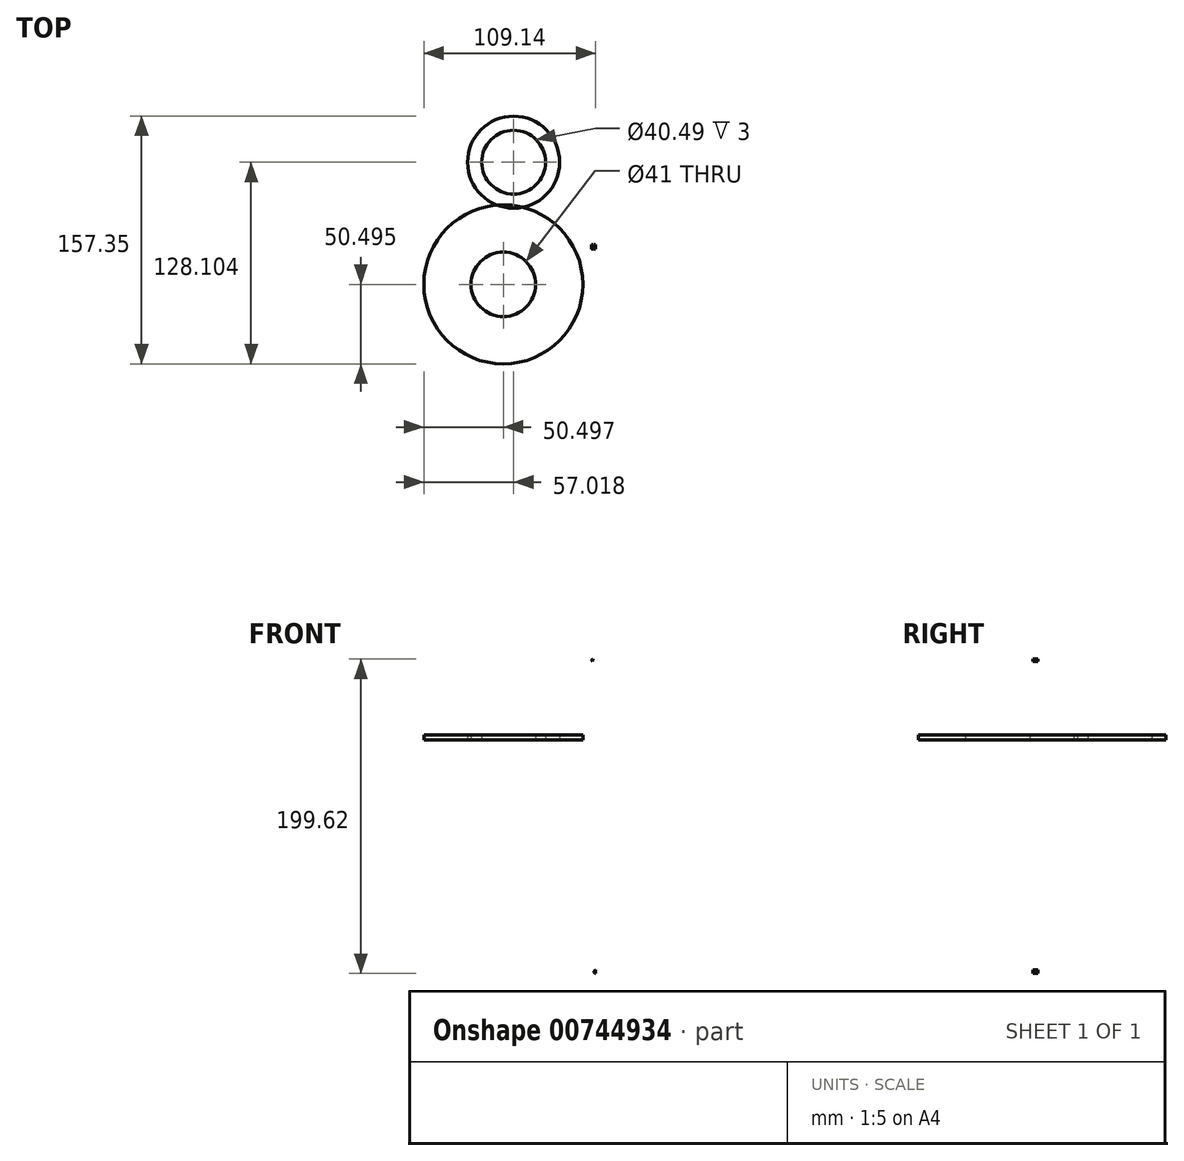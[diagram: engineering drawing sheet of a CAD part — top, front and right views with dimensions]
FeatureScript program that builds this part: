
annotation { "Feature Type Name" : "Feature", "Feature Type Description" : "" }
export const myFeature = defineFeature(function(context is Context, id is Id, definition is map)
    precondition{}
    {
        {
            var Q0;
            Q0=qCreatedBy(makeId("Front.planeOp"),FACE);
            var sketch = newSketch(context, id + "F0", { "sketchPlane" : qUnion([Q0])});
            skFitSpline(sketch, "E0", {"points": [v(18.94, 55.8) * mm, v(19.4, 42.74) * mm, v(74.56, -23) * mm, v(58.26, -54.69) * mm, v(18.93, -151.45) * mm], "startDerivative": vector(-29.4, -78.93) * mm, "endDerivative": vector(0, -157.02) * mm});
            skFitSpline(sketch, "E1.0", {"points": [v(9.57, 59.29) * mm, v(9.44, 58.92) * mm, v(9.1, 58.03) * mm, v(8.45, 56.18) * mm, v(7.84, 53.83) * mm, v(7.44, 51.02) * mm, v(7.45, 47.87) * mm, v(7.89, 45.1) * mm, v(8.5, 42.89) * mm, v(9.08, 41.22) * mm, v(9.67, 39.84) * mm, v(10.2, 38.74) * mm, v(10.64, 37.9) * mm, v(11.1, 37.1) * mm, v(11.72, 36.02) * mm, v(12.56, 34.7) * mm, v(13.65, 33.11) * mm, v(15.19, 31) * mm, v(17.29, 28.36) * mm, v(20.06, 25.1) * mm, v(23.05, 21.77) * mm, v(27.29, 17.22) * mm, v(32.95, 11.36) * mm, v(39.98, 4.2) * mm, v(46.9, -2.94) * mm, v(53.3, -9.85) * mm, v(57.89, -15.23) * mm, v(60.89, -19.14) * mm, v(62.74, -21.82) * mm, v(63.91, -23.77) * mm, v(64.6, -25.1) * mm, v(64.93, -25.82) * mm, v(65.13, -26.31) * mm, v(65.28, -26.74) * mm, v(65.42, -27.2) * mm, v(65.51, -27.62) * mm, v(65.56, -28.04) * mm, v(65.56, -28.36) * mm, v(65.5, -28.75) * mm, v(65.26, -29.42) * mm, v(64.73, -30.46) * mm, v(63.8, -31.88) * mm, v(62.48, -33.62) * mm, v(60.8, -35.67) * mm, v(58.8, -38.02) * mm, v(56.54, -40.67) * mm, v(54.08, -43.65) * mm, v(51.92, -46.42) * mm, v(50.14, -48.83) * mm, v(48.36, -51.35) * mm, v(46.15, -54.66) * mm, v(43.52, -58.88) * mm, v(40.9, -63.31) * mm, v(37.47, -69.48) * mm, v(33.27, -77.6) * mm, v(28.46, -87.76) * mm, v(23.96, -98.1) * mm, v(19.86, -108.39) * mm, v(16.26, -118.37) * mm, v(13.25, -127.84) * mm, v(11.3, -135.12) * mm, v(10.14, -140.51) * mm, v(9.48, -144.34) * mm, v(9.04, -147.97) * mm, v(8.93, -150.3) * mm, v(8.93, -151.45) * mm]});
            skLineSegment(sketch, "E2", {"start": v(18.94, 55.8) * mm, "end": v(8.37, 55.8) * mm});
            skLineSegment(sketch, "E3", {"start": v(18.93, -151.45) * mm, "end": v(8.93, -151.45) * mm});
            skLineSegment(sketch, "E4", {"start": v(14.05, 32.57) * mm, "end": v(16.18, 32.57) * mm});
            skFitSpline(sketch, "E5.trimOffspring", {"points": [v(9.57, 59.29) * mm, v(9.44, 58.92) * mm, v(9.1, 58.03) * mm, v(8.45, 56.18) * mm, v(7.84, 53.83) * mm, v(7.44, 51.02) * mm, v(7.45, 47.87) * mm, v(7.89, 45.1) * mm, v(8.5, 42.89) * mm, v(9.08, 41.22) * mm, v(9.67, 39.84) * mm, v(10.2, 38.74) * mm, v(10.64, 37.9) * mm, v(11.1, 37.1) * mm, v(11.72, 36.02) * mm, v(12.56, 34.7) * mm, v(13.65, 33.11) * mm, v(15.19, 31) * mm, v(17.29, 28.36) * mm, v(20.06, 25.1) * mm, v(23.05, 21.77) * mm, v(27.29, 17.22) * mm, v(32.95, 11.36) * mm, v(39.98, 4.2) * mm, v(46.9, -2.94) * mm, v(53.3, -9.85) * mm, v(57.89, -15.23) * mm, v(60.89, -19.14) * mm, v(62.74, -21.82) * mm, v(63.91, -23.77) * mm, v(64.6, -25.1) * mm, v(64.93, -25.82) * mm, v(65.13, -26.31) * mm, v(65.28, -26.74) * mm, v(65.42, -27.2) * mm, v(65.51, -27.62) * mm, v(65.56, -28.04) * mm, v(65.56, -28.36) * mm, v(65.5, -28.75) * mm, v(65.26, -29.42) * mm, v(64.73, -30.46) * mm, v(63.8, -31.88) * mm, v(62.48, -33.62) * mm, v(60.8, -35.67) * mm, v(58.8, -38.02) * mm, v(56.54, -40.67) * mm, v(54.08, -43.65) * mm, v(51.92, -46.42) * mm, v(50.14, -48.83) * mm, v(48.36, -51.35) * mm, v(46.15, -54.66) * mm, v(43.52, -58.88) * mm, v(40.9, -63.31) * mm, v(37.47, -69.48) * mm, v(33.27, -77.6) * mm, v(28.46, -87.76) * mm, v(23.96, -98.1) * mm, v(19.86, -108.39) * mm, v(16.26, -118.37) * mm, v(13.25, -127.84) * mm, v(11.3, -135.12) * mm, v(10.14, -140.51) * mm, v(9.48, -144.34) * mm, v(9.04, -147.97) * mm, v(8.93, -150.3) * mm, v(8.93, -151.45) * mm]});
            skFitSpline(sketch, "E6.trimOffspring", {"points": [v(9.57, 59.29) * mm, v(9.44, 58.92) * mm, v(9.1, 58.03) * mm, v(8.45, 56.18) * mm, v(7.84, 53.83) * mm, v(7.44, 51.02) * mm, v(7.45, 47.87) * mm, v(7.89, 45.1) * mm, v(8.5, 42.89) * mm, v(9.08, 41.22) * mm, v(9.67, 39.84) * mm, v(10.2, 38.74) * mm, v(10.64, 37.9) * mm, v(11.1, 37.1) * mm, v(11.72, 36.02) * mm, v(12.56, 34.7) * mm, v(13.65, 33.11) * mm, v(15.19, 31) * mm, v(17.29, 28.36) * mm, v(20.06, 25.1) * mm, v(23.05, 21.77) * mm, v(27.29, 17.22) * mm, v(32.95, 11.36) * mm, v(39.98, 4.2) * mm, v(46.9, -2.94) * mm, v(53.3, -9.85) * mm, v(57.89, -15.23) * mm, v(60.89, -19.14) * mm, v(62.74, -21.82) * mm, v(63.91, -23.77) * mm, v(64.6, -25.1) * mm, v(64.93, -25.82) * mm, v(65.13, -26.31) * mm, v(65.28, -26.74) * mm, v(65.42, -27.2) * mm, v(65.51, -27.62) * mm, v(65.56, -28.04) * mm, v(65.56, -28.36) * mm, v(65.5, -28.75) * mm, v(65.26, -29.42) * mm, v(64.73, -30.46) * mm, v(63.8, -31.88) * mm, v(62.48, -33.62) * mm, v(60.8, -35.67) * mm, v(58.8, -38.02) * mm, v(56.54, -40.67) * mm, v(54.08, -43.65) * mm, v(51.92, -46.42) * mm, v(50.14, -48.83) * mm, v(48.36, -51.35) * mm, v(46.15, -54.66) * mm, v(43.52, -58.88) * mm, v(40.9, -63.31) * mm, v(37.47, -69.48) * mm, v(33.27, -77.6) * mm, v(28.46, -87.76) * mm, v(23.96, -98.1) * mm, v(19.86, -108.39) * mm, v(16.26, -118.37) * mm, v(13.25, -127.84) * mm, v(11.3, -135.12) * mm, v(10.14, -140.51) * mm, v(9.48, -144.34) * mm, v(9.04, -147.97) * mm, v(8.93, -150.3) * mm, v(8.93, -151.45) * mm]});
            skLineSegment(sketch, "E7", {"start": v(42.73, 1.36) * mm, "end": v(42.73, 1.36) * mm});
            skPoint(sketch, "E8.orphan", {"position": v(0, -86.14) * mm});
            skPoint(sketch, "E9.end.orphan", {"position": v(15.52, -133.04) * mm});
            skFitSpline(sketch, "E10.trimOffspring", {"points": [v(9.57, 59.29) * mm, v(9.44, 58.92) * mm, v(9.1, 58.03) * mm, v(8.45, 56.18) * mm, v(7.84, 53.83) * mm, v(7.44, 51.02) * mm, v(7.45, 47.87) * mm, v(7.89, 45.1) * mm, v(8.5, 42.89) * mm, v(9.08, 41.22) * mm, v(9.67, 39.84) * mm, v(10.2, 38.74) * mm, v(10.64, 37.9) * mm, v(11.1, 37.1) * mm, v(11.72, 36.02) * mm, v(12.56, 34.7) * mm, v(13.65, 33.11) * mm, v(15.19, 31) * mm, v(17.29, 28.36) * mm, v(20.06, 25.1) * mm, v(23.05, 21.77) * mm, v(27.29, 17.22) * mm, v(32.95, 11.36) * mm, v(39.98, 4.2) * mm, v(46.9, -2.94) * mm, v(53.3, -9.85) * mm, v(57.89, -15.23) * mm, v(60.89, -19.14) * mm, v(62.74, -21.82) * mm, v(63.91, -23.77) * mm, v(64.6, -25.1) * mm, v(64.93, -25.82) * mm, v(65.13, -26.31) * mm, v(65.28, -26.74) * mm, v(65.42, -27.2) * mm, v(65.51, -27.62) * mm, v(65.56, -28.04) * mm, v(65.56, -28.36) * mm, v(65.5, -28.75) * mm, v(65.26, -29.42) * mm, v(64.73, -30.46) * mm, v(63.8, -31.88) * mm, v(62.48, -33.62) * mm, v(60.8, -35.67) * mm, v(58.8, -38.02) * mm, v(56.54, -40.67) * mm, v(54.08, -43.65) * mm, v(51.92, -46.42) * mm, v(50.14, -48.83) * mm, v(48.36, -51.35) * mm, v(46.15, -54.66) * mm, v(43.52, -58.88) * mm, v(40.9, -63.31) * mm, v(37.47, -69.48) * mm, v(33.27, -77.6) * mm, v(28.46, -87.76) * mm, v(23.96, -98.1) * mm, v(19.86, -108.39) * mm, v(16.26, -118.37) * mm, v(13.25, -127.84) * mm, v(11.3, -135.12) * mm, v(10.14, -140.51) * mm, v(9.48, -144.34) * mm, v(9.04, -147.97) * mm, v(8.93, -150.3) * mm, v(8.93, -151.45) * mm]});
            skLineSegment(sketch, "E11", {"start": v(14.05, 32.57) * mm, "end": v(21.01, 32.57) * mm});
            skLineSegment(sketch, "E12", {"start": v(21.01, 32.57) * mm, "end": v(21.01, 29.66) * mm});
            skLineSegment(sketch, "E13", {"start": v(21.01, 29.66) * mm, "end": v(16.36, 29.66) * mm});
            skLineSegment(sketch, "E14", {"start": v(59.17, -16.92) * mm, "end": v(59.17, -16.92) * mm});
            skFitSpline(sketch, "E15.trimOffspring", {"points": [v(9.57, 59.29) * mm, v(9.44, 58.92) * mm, v(9.1, 58.03) * mm, v(8.45, 56.18) * mm, v(7.84, 53.83) * mm, v(7.44, 51.02) * mm, v(7.45, 47.87) * mm, v(7.89, 45.1) * mm, v(8.5, 42.89) * mm, v(9.08, 41.22) * mm, v(9.67, 39.84) * mm, v(10.2, 38.74) * mm, v(10.64, 37.9) * mm, v(11.1, 37.1) * mm, v(11.72, 36.02) * mm, v(12.56, 34.7) * mm, v(13.65, 33.11) * mm, v(15.19, 31) * mm, v(17.29, 28.36) * mm, v(20.06, 25.1) * mm, v(23.05, 21.77) * mm, v(27.29, 17.22) * mm, v(32.95, 11.36) * mm, v(39.98, 4.2) * mm, v(46.9, -2.94) * mm, v(53.3, -9.85) * mm, v(57.89, -15.23) * mm, v(60.89, -19.14) * mm, v(62.74, -21.82) * mm, v(63.91, -23.77) * mm, v(64.6, -25.1) * mm, v(64.93, -25.82) * mm, v(65.13, -26.31) * mm, v(65.28, -26.74) * mm, v(65.42, -27.2) * mm, v(65.51, -27.62) * mm, v(65.56, -28.04) * mm, v(65.56, -28.36) * mm, v(65.5, -28.75) * mm, v(65.26, -29.42) * mm, v(64.73, -30.46) * mm, v(63.8, -31.88) * mm, v(62.48, -33.62) * mm, v(60.8, -35.67) * mm, v(58.8, -38.02) * mm, v(56.54, -40.67) * mm, v(54.08, -43.65) * mm, v(51.92, -46.42) * mm, v(50.14, -48.83) * mm, v(48.36, -51.35) * mm, v(46.15, -54.66) * mm, v(43.52, -58.88) * mm, v(40.9, -63.31) * mm, v(37.47, -69.48) * mm, v(33.27, -77.6) * mm, v(28.46, -87.76) * mm, v(23.96, -98.1) * mm, v(19.86, -108.39) * mm, v(16.26, -118.37) * mm, v(13.25, -127.84) * mm, v(11.3, -135.12) * mm, v(10.14, -140.51) * mm, v(9.48, -144.34) * mm, v(9.04, -147.97) * mm, v(8.93, -150.3) * mm, v(8.93, -151.45) * mm]});
            skLineSegment(sketch, "E16", {"start": v(15.52, -120.8) * mm, "end": v(18.75, -120.8) * mm});
            skLineSegment(sketch, "E17", {"start": v(18.75, -123.72) * mm, "end": v(14.58, -123.72) * mm});
            skLineSegment(sketch, "E18", {"start": v(58.14, -15.63) * mm, "end": v(58.14, -15.63) * mm});
            skPoint(sketch, "E19.end.orphan", {"position": v(28.86, -104.28) * mm});
            skPoint(sketch, "E19.start.orphan", {"position": v(28.86, -101.3) * mm});
            skFitSpline(sketch, "E20.trimOffspring", {"points": [v(9.57, 59.29) * mm, v(9.44, 58.92) * mm, v(9.1, 58.03) * mm, v(8.45, 56.18) * mm, v(7.84, 53.83) * mm, v(7.44, 51.02) * mm, v(7.45, 47.87) * mm, v(7.89, 45.1) * mm, v(8.5, 42.89) * mm, v(9.08, 41.22) * mm, v(9.67, 39.84) * mm, v(10.2, 38.74) * mm, v(10.64, 37.9) * mm, v(11.1, 37.1) * mm, v(11.72, 36.02) * mm, v(12.56, 34.7) * mm, v(13.65, 33.11) * mm, v(15.19, 31) * mm, v(17.29, 28.36) * mm, v(20.06, 25.1) * mm, v(23.05, 21.77) * mm, v(27.29, 17.22) * mm, v(32.95, 11.36) * mm, v(39.98, 4.2) * mm, v(46.9, -2.94) * mm, v(53.3, -9.85) * mm, v(57.89, -15.23) * mm, v(60.89, -19.14) * mm, v(62.74, -21.82) * mm, v(63.91, -23.77) * mm, v(64.6, -25.1) * mm, v(64.93, -25.82) * mm, v(65.13, -26.31) * mm, v(65.28, -26.74) * mm, v(65.42, -27.2) * mm, v(65.51, -27.62) * mm, v(65.56, -28.04) * mm, v(65.56, -28.36) * mm, v(65.5, -28.75) * mm, v(65.26, -29.42) * mm, v(64.73, -30.46) * mm, v(63.8, -31.88) * mm, v(62.48, -33.62) * mm, v(60.8, -35.67) * mm, v(58.8, -38.02) * mm, v(56.54, -40.67) * mm, v(54.08, -43.65) * mm, v(51.92, -46.42) * mm, v(50.14, -48.83) * mm, v(48.36, -51.35) * mm, v(46.15, -54.66) * mm, v(43.52, -58.88) * mm, v(40.9, -63.31) * mm, v(37.47, -69.48) * mm, v(33.27, -77.6) * mm, v(28.46, -87.76) * mm, v(23.96, -98.1) * mm, v(19.86, -108.39) * mm, v(16.26, -118.37) * mm, v(13.25, -127.84) * mm, v(11.3, -135.12) * mm, v(10.14, -140.51) * mm, v(9.48, -144.34) * mm, v(9.04, -147.97) * mm, v(8.93, -150.3) * mm, v(8.93, -151.45) * mm]});
            skLineSegment(sketch, "E21", {"start": v(18.75, -120.8) * mm, "end": v(20.6, -120.8) * mm});
            skLineSegment(sketch, "E22", {"start": v(20.6, -120.8) * mm, "end": v(20.6, -123.72) * mm});
            skLineSegment(sketch, "E23", {"start": v(20.6, -123.72) * mm, "end": v(18.75, -123.72) * mm});
            skLineSegment(sketch, "E24", {"start": v(17.74, 29.66) * mm, "end": v(16.27, 29.66) * mm});
            skFitSpline(sketch, "E25", {"points": [v(17.59, 51.26) * mm, v(16.83, 50.41) * mm, v(17.46, 49.64) * mm], "startDerivative": vector(-2.22, -1.65) * mm, "endDerivative": vector(2, -1.58) * mm});
            skFitSpline(sketch, "E26", {"points": [v(19.35, -146.2) * mm, v(18.22, -147.38) * mm, v(19.1, -148.36) * mm], "startDerivative": vector(-3.21, -2.27) * mm, "endDerivative": vector(2.83, -2.03) * mm});
            skSolve(sketch);
        }
        {
            var Q0;
            Q0 = qSketchRegion(id + "F0", true);
            extrude(context, id + "F1", {"entities" : qUnion([Q0]), "depth" : 3 * mm, "offsetDistance" : 25 * mm});
        }
        {
            var Q0;
            Q0=qCreatedBy(makeId("Top.planeOp"),FACE);
            var sketch = newSketch(context, id + "F2", { "sketchPlane" : qUnion([Q0])});
            skCircle(sketch, "E27", {"center": v(-39.3, -25.43) * mm, "radius": 20.5 * mm});
            skCircle(sketch, "E28", {"center": v(-39.3, -25.43) * mm, "radius": 50.5 * mm});
            skSolve(sketch);
        }
        {
            var Q0;
            Q0 = qSketchRegion(id + "F2", true);
            extrude(context, id + "F3", {"entities" : qUnion([Q0]), "depth" : 3 * mm, "offsetDistance" : 25 * mm});
        }
        {
            var Q0;
            Q0=qCreatedBy(makeId("Top.planeOp"),FACE);
            var sketch = newSketch(context, id + "F4", { "sketchPlane" : qUnion([Q0])});
            skCircle(sketch, "E29", {"center": v(-32.77, 52.17) * mm, "radius": 20.25 * mm});
            skCircle(sketch, "E30", {"center": v(-32.77, 52.17) * mm, "radius": 29.25 * mm});
            skSolve(sketch);
        }
        {
            var Q0;
            Q0 = qSketchRegion(id + "F4", true);
            extrude(context, id + "F5", {"entities" : qUnion([Q0]), "depth" : 3 * mm, "offsetDistance" : 25 * mm});
        }
    });
